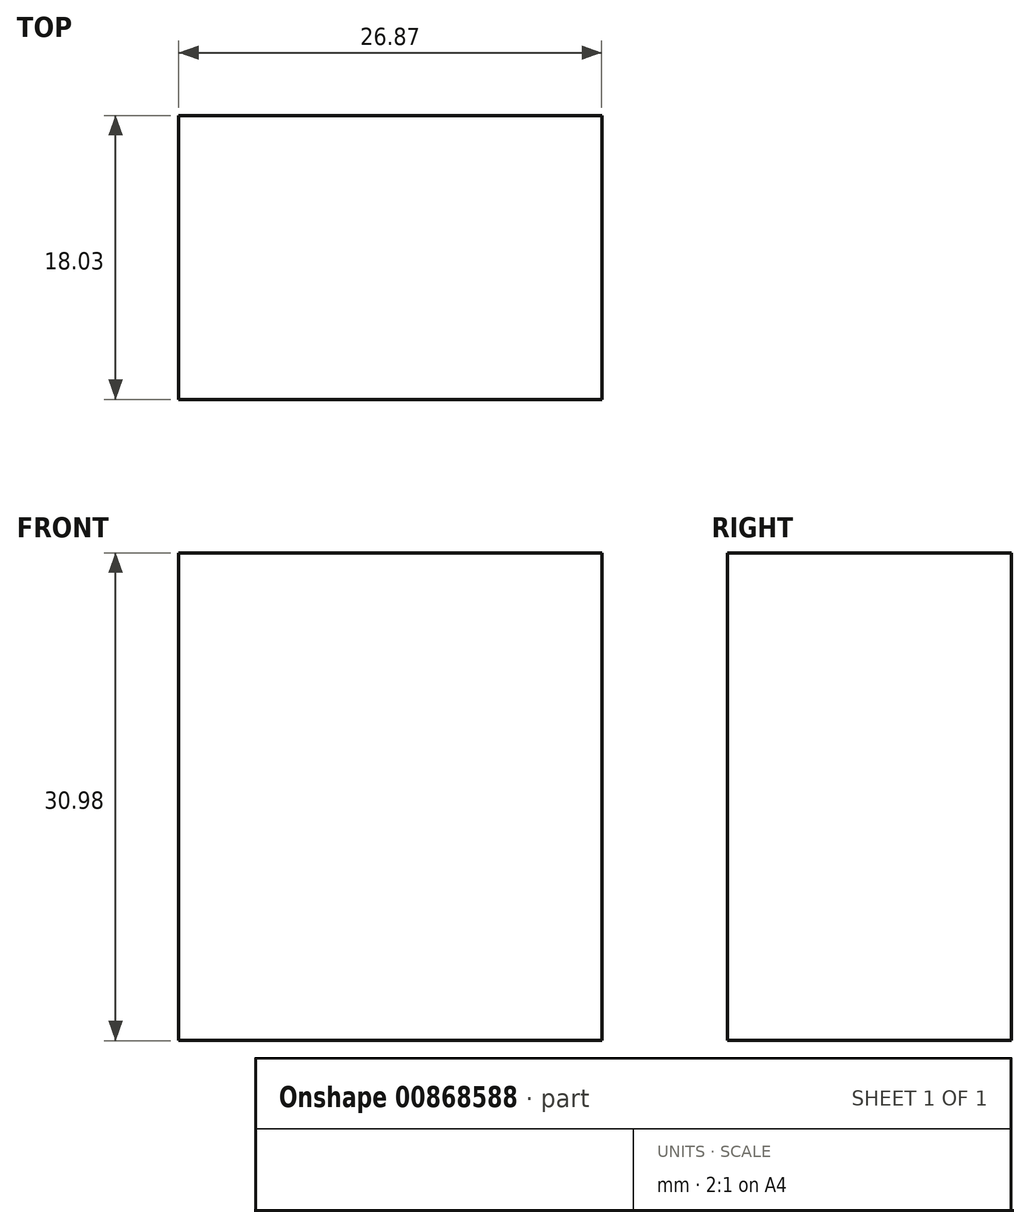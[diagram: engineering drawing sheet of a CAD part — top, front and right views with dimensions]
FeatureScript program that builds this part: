
annotation { "Feature Type Name" : "Feature", "Feature Type Description" : "" }
export const myFeature = defineFeature(function(context is Context, id is Id, definition is map)
    precondition{}
    {
        {
            var Q0;
            Q0=qCreatedBy(makeId("Front.planeOp"),FACE);
            var sketch = newSketch(context, id + "F0", { "sketchPlane" : qUnion([Q0])});
            skLineSegment(sketch, "E0.bottom", {"start": v(-15.64, 36.34) * mm, "end": v(11.23, 36.34) * mm});
            skLineSegment(sketch, "E0.top", {"start": v(-15.64, 5.36) * mm, "end": v(11.23, 5.36) * mm});
            skLineSegment(sketch, "E0.left", {"start": v(-15.64, 36.34) * mm, "end": v(-15.64, 5.36) * mm});
            skLineSegment(sketch, "E0.right", {"start": v(11.23, 36.34) * mm, "end": v(11.23, 5.36) * mm});
            skSolve(sketch);
        }
        {
            var Q0;
            Q0 = qSketchRegion(id + "F0", true);
            extrude(context, id + "F1", {"entities" : qUnion([Q0]), "depth" : 18.03 * mm, "offsetDistance" : 25.4 * mm});
        }
    });
